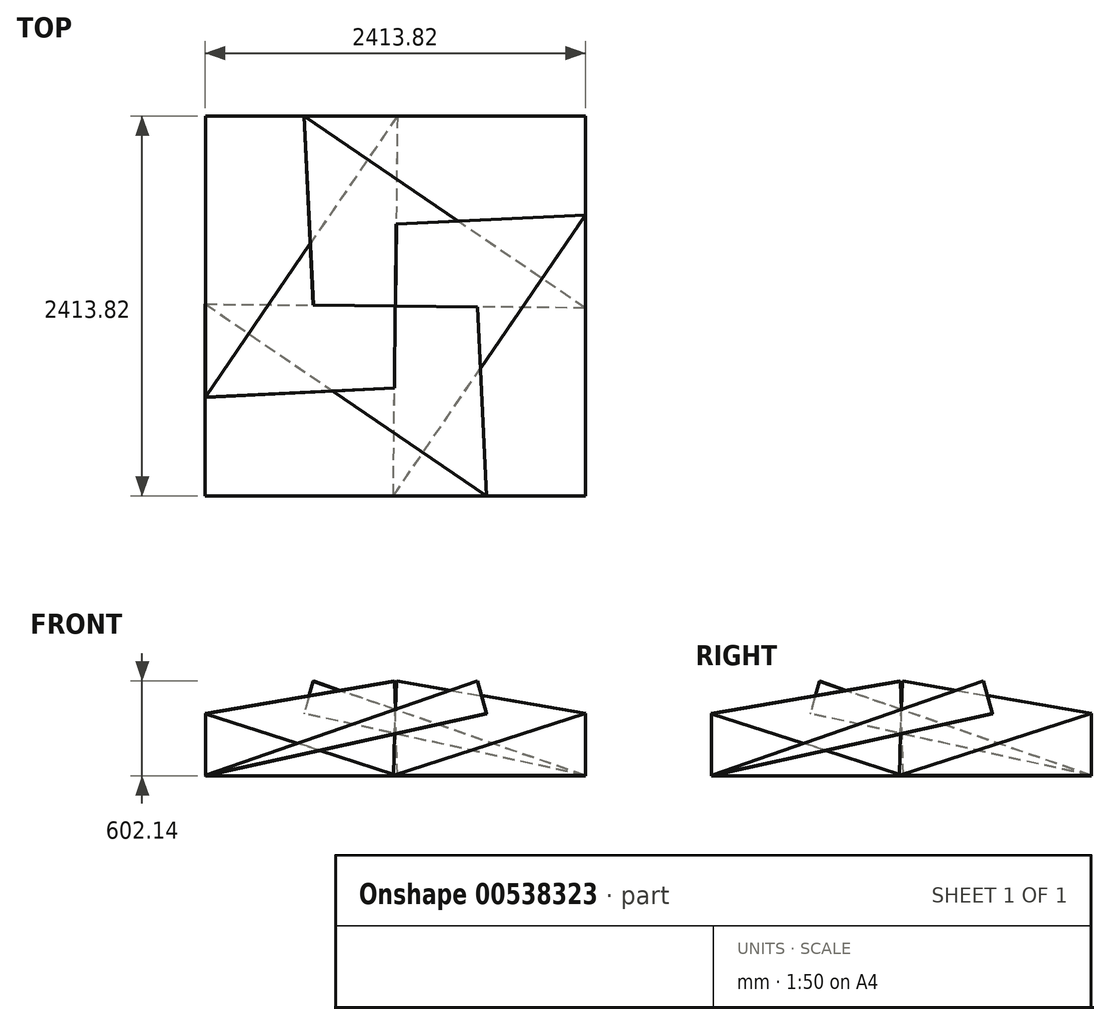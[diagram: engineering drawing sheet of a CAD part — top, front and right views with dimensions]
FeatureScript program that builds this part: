
annotation { "Feature Type Name" : "Feature", "Feature Type Description" : "" }
export const myFeature = defineFeature(function(context is Context, id is Id, definition is map)
    precondition{}
    {
        {
            var Q0;
            Q0=qCreatedBy(makeId("Front.planeOp"),FACE);
            var sketch = newSketch(context, id + "F0", { "sketchPlane" : qUnion([Q0])});
            skLineSegment(sketch, "E0", {"start": v(0, 0) * mm, "end": v(0, 505.37) * mm});
            skSolve(sketch);
        }
        {
            var Q0;
            Q0=qCreatedBy(makeId("Top.planeOp"),FACE);
            var sketch = newSketch(context, id + "F1", { "sketchPlane" : qUnion([Q0])});
            skLineSegment(sketch, "E1.bottom", {"start": v(-1206.5, 1206.5) * mm, "end": v(1206.5, 1206.5) * mm, "construction": true});
            skLineSegment(sketch, "E1.top", {"start": v(-1206.5, -1206.5) * mm, "end": v(1206.5, -1206.5) * mm, "construction": true});
            skLineSegment(sketch, "E1.left", {"start": v(-1206.5, 1206.5) * mm, "end": v(-1206.5, -1206.5) * mm, "construction": true});
            skLineSegment(sketch, "E1.right", {"start": v(1206.5, 1206.5) * mm, "end": v(1206.5, -1206.5) * mm, "construction": true});
            skLineSegment(sketch, "E2", {"start": v(-1206.5, 1206.5) * mm, "end": v(0, 0) * mm, "construction": true});
            skLineSegment(sketch, "E3", {"start": v(0, 0) * mm, "end": v(1206.5, 1206.5) * mm, "construction": true});
            skLineSegment(sketch, "E4", {"start": v(1206.5, -1206.5) * mm, "end": v(0, 0) * mm, "construction": true});
            skLineSegment(sketch, "E5", {"start": v(-1206.5, -1206.5) * mm, "end": v(0, 0) * mm, "construction": true});
            skSolve(sketch);
        }
        {
            var Q0;
            Q0=sQuery(id+"F1.wireOp",EDGE,"E1.right");
            var Q1;
            Q1=qCreatedBy(makeId("Right.planeOp"),FACE);
            var Q2;
            Q2 = qBodyType(qCreatedBy(id + "F3" ,EDGE), BodyType.WIRE);
            cPlane(context, id + "F2", {"entities" : qUnion([Q0, Q1, Q2]), "cplaneType" : CPlaneType.LINE_ANGLE, "offset" : 25.4 * mm, "angle" : 0 * degree, "width" : 152.4 * mm, "height" : 152.4 * mm});
        }
        {
            var Q0;
            Q0=qCreatedBy(id+"F2.planeOp",FACE);
            var sketch = newSketch(context, id + "F3", { "sketchPlane" : qUnion([Q0])});
            skPoint(sketch, "E6.0", {"position": v(1206.5, 0) * mm});
            skPoint(sketch, "E7.0", {"position": v(0, 0) * mm});
            skPoint(sketch, "E8.0", {"position": v(-1206.5, 0) * mm});
            skLineSegment(sketch, "E9", {"start": v(1206.5, 0) * mm, "end": v(1206.5, 1828.8) * mm, "construction": true});
            skLineSegment(sketch, "E10", {"start": v(-1206.5, 2362.2) * mm, "end": v(-1206.5, 0) * mm, "construction": true});
            skLineSegment(sketch, "E11", {"start": v(-1206.5, 1828.8) * mm, "end": v(12.7, 1828.8) * mm, "construction": true});
            skLineSegment(sketch, "E12", {"start": v(1206.5, 1828.8) * mm, "end": v(-579.2, 2223.53) * mm});
            skLineSegment(sketch, "E13", {"start": v(-579.2, 2223.53) * mm, "end": v(-1206.5, 2362.2) * mm, "construction": true});
            skLineSegment(sketch, "E14", {"start": v(12.7, 1828.8) * mm, "end": v(12.7, 2092.7) * mm, "construction": true});
            skLineSegment(sketch, "E15", {"start": v(12.7, 1828.8) * mm, "end": v(1206.5, 1828.8) * mm, "construction": true});
            skLineSegment(sketch, "E16", {"start": v(-1206.5, 2362.2) * mm, "end": v(-1206.5, 2895.6) * mm, "construction": true});
            skCircle(sketch, "E17", {"center": v(-1206.5, 2362.2) * mm, "radius": 533.4 * mm, "construction": true});
            skSolve(sketch);
        }
        {
            var Q0;
            Q0=sQuery(id+"F1.wireOp",EDGE,"E1.bottom");
            var Q1;
            Q1=qCreatedBy(makeId("Front.planeOp"),FACE);
            cPlane(context, id + "F4", {"entities" : qUnion([Q0, Q1]), "cplaneType" : CPlaneType.LINE_ANGLE, "offset" : 25.4 * mm, "angle" : 0 * degree, "width" : 152.4 * mm, "height" : 152.4 * mm});
        }
        {
            var Q0;
            Q0=qCreatedBy(id+"F4.planeOp",FACE);
            var sketch = newSketch(context, id + "F5", { "sketchPlane" : qUnion([Q0])});
            skPoint(sketch, "E18.0", {"position": v(-1206.5, 2895.6) * mm});
            skPoint(sketch, "E19.0", {"position": v(-1206.5, 0) * mm});
            skPoint(sketch, "E20.0", {"position": v(1206.5, 0) * mm});
            skPoint(sketch, "E21.0", {"position": v(0, 0) * mm});
            skLineSegment(sketch, "E22.bottom", {"start": v(-1206.5, 2895.6) * mm, "end": v(1206.5, 2895.6) * mm, "construction": true});
            skLineSegment(sketch, "E22.top", {"start": v(-1206.5, 0) * mm, "end": v(1206.5, 0) * mm, "construction": true});
            skLineSegment(sketch, "E22.left", {"start": v(-1206.5, 2895.6) * mm, "end": v(-1206.5, 0) * mm, "construction": true});
            skLineSegment(sketch, "E22.right", {"start": v(1206.5, 2895.6) * mm, "end": v(1206.5, 0) * mm, "construction": true});
            skSolve(sketch);
        }
        {
            var Q0;
            Q0=sQuery(id+"F1.wireOp",EDGE,"E1.top");
            var Q1;
            Q1=qCreatedBy(makeId("Front.planeOp"),FACE);
            cPlane(context, id + "F6", {"entities" : qUnion([Q0, Q1]), "cplaneType" : CPlaneType.LINE_ANGLE, "offset" : 25.4 * mm, "angle" : 0 * degree, "width" : 152.4 * mm, "height" : 152.4 * mm});
        }
        {
            var Q0;
            Q0=qCreatedBy(id+"F6.planeOp",FACE);
            var sketch = newSketch(context, id + "F7", { "sketchPlane" : qUnion([Q0])});
            skPoint(sketch, "E23.0", {"position": v(-1206.5, 1828.8) * mm});
            skPoint(sketch, "E24.0", {"position": v(-1206.5, 0) * mm});
            skPoint(sketch, "E25.0", {"position": v(1206.5, 0) * mm});
            skPoint(sketch, "E26.0", {"position": v(0, 0) * mm});
            skLineSegment(sketch, "E27.bottom", {"start": v(1206.5, 0) * mm, "end": v(-1206.5, 0) * mm, "construction": true});
            skLineSegment(sketch, "E27.top", {"start": v(1206.5, 1828.8) * mm, "end": v(-1206.5, 1828.8) * mm, "construction": true});
            skLineSegment(sketch, "E27.left", {"start": v(1206.5, 0) * mm, "end": v(1206.5, 1828.8) * mm, "construction": true});
            skLineSegment(sketch, "E27.right", {"start": v(-1206.5, 0) * mm, "end": v(-1206.5, 1828.8) * mm, "construction": true});
            skLineSegment(sketch, "E28", {"start": v(12.7, 1828.8) * mm, "end": v(12.7, 0) * mm, "construction": true});
            skSolve(sketch);
        }
        {
            var Q0;
            Q0=sQuery(id+"F7.wireOp",EDGE,"E27.top");
            cPoint(context, id + "F8", {"entities" : qUnion([Q0]), "parameter" : 0.5});
        }
        {
            var Q0;
            Q0=sQuery(id+"F3.wireOp",VERTEX,"E13.start");
            var Q1;
            Q1 = qCreatedBy(id + "F8" ,VERTEX);
            var Q2;
            Q2=sQuery(id+"F7.wireOp",VERTEX,"E23.0");
            cPlane(context, id + "F9", {"entities" : qUnion([Q0, Q1, Q2]), "cplaneType" : CPlaneType.THREE_POINT, "offset" : 25.4 * mm, "width" : 152.4 * mm, "height" : 152.4 * mm});
        }
        {
            var Q0;
            Q0=qCreatedBy(id+"F9.planeOp",FACE);
            var sketch = newSketch(context, id + "F10", { "sketchPlane" : qUnion([Q0])});
            skPoint(sketch, "E29.0", {"position": v(-12.7, 783.33) * mm});
            skPoint(sketch, "E30.0", {"position": v(1206.5, -1045.47) * mm});
            skPoint(sketch, "E31.0", {"position": v(1206.5, 783.33) * mm});
            skLineSegment(sketch, "E32", {"start": v(-12.7, 783.33) * mm, "end": v(1206.5, -1045.47) * mm});
            skLineSegment(sketch, "E33", {"start": v(1206.5, 783.33) * mm, "end": v(-12.7, 783.33) * mm});
            skLineSegment(sketch, "E34", {"start": v(1206.5, -1045.47) * mm, "end": v(1206.5, 783.33) * mm});
            skSolve(sketch);
        }
        {
            var Q0;
            Q0=sQuery(id+"F10.wireOp",VERTEX,"E30.0");
            var Q1;
            Q1=sQuery(id+"F5.wireOp",VERTEX,"E22.right.start");
            var Q2;
            Q2=sQuery(id+"F10.wireOp",VERTEX,"E29.0");
            cPlane(context, id + "F11", {"entities" : qUnion([Q0, Q1, Q2]), "cplaneType" : CPlaneType.THREE_POINT, "offset" : 25.4 * mm, "width" : 152.4 * mm, "height" : 152.4 * mm});
        }
        {
            var Q0;
            Q0=qCreatedBy(id+"F11.planeOp",FACE);
            var sketch = newSketch(context, id + "F12", { "sketchPlane" : qUnion([Q0])});
            skPoint(sketch, "E35.0", {"position": v(-1595.64, -2093.72) * mm});
            skPoint(sketch, "E36.0", {"position": v(854.97, -1279.9) * mm});
            skPoint(sketch, "E37.0", {"position": v(-383.23, 536.08) * mm});
            skLineSegment(sketch, "E38", {"start": v(854.97, -1279.9) * mm, "end": v(-383.23, 536.08) * mm});
            skLineSegment(sketch, "E39", {"start": v(-383.23, 536.08) * mm, "end": v(-364.16, -1292.62) * mm});
            skLineSegment(sketch, "E40", {"start": v(-364.16, -1292.62) * mm, "end": v(854.97, -1279.9) * mm});
            skSolve(sketch);
        }
        {
            var Q0;
            Q0=makeQuery(id+"F12.imprint","IMPRINT",FACE,{"disambiguationData":[TD([[makeQuery(id+"F12.imprint","IMPRINT",EDGE,{"derivedFrom":sQuery(id+"F12.wireOp",EDGE,"E38")}),1.0]])]});
            var Q1;
            Q1=makeQuery(id+"F10.imprint","IMPRINT",FACE,{"disambiguationData":[TD([[makeQuery(id+"F10.imprint","IMPRINT",EDGE,{"derivedFrom":sQuery(id+"F10.wireOp",EDGE,"E32")}),1.0]])]});
            extrude(context, id + "F13", {"entities" : qUnion([Q0, Q1]), "endBound" : BoundingType.SYMMETRIC, "oppositeDirection" : true, "depth" : 2.54 * mm, "offsetDistance" : 25.4 * mm});
        }
        {
            var Q0;
            Q0=makeQuery(id+"F13.opExtrude","SWEPT_BODY",BODY,{"disambiguationData":[OSD([sQuery(id+"F12.wireOp",EDGE,"E38"),sQuery(id+"F12.wireOp",EDGE,"E39"),sQuery(id+"F12.wireOp",EDGE,"E40")])]});
            var Q1;
            Q1=makeQuery(id+"F13.opExtrude","SWEPT_BODY",BODY,{"disambiguationData":[OSD([sQuery(id+"F10.wireOp",EDGE,"E32"),sQuery(id+"F10.wireOp",EDGE,"E33"),sQuery(id+"F10.wireOp",EDGE,"E34")])]});
            var Q2;
            Q2=sQuery(id+"F0.wireOp",EDGE,"E0");
            circularPattern(context, id + "F14", {"entities" : qUnion([Q0, Q1]), "axis" : qUnion([Q2]), "angle" : 360 * degree, "instanceCount" : 4, "equalSpace" : true});
        }
    });
